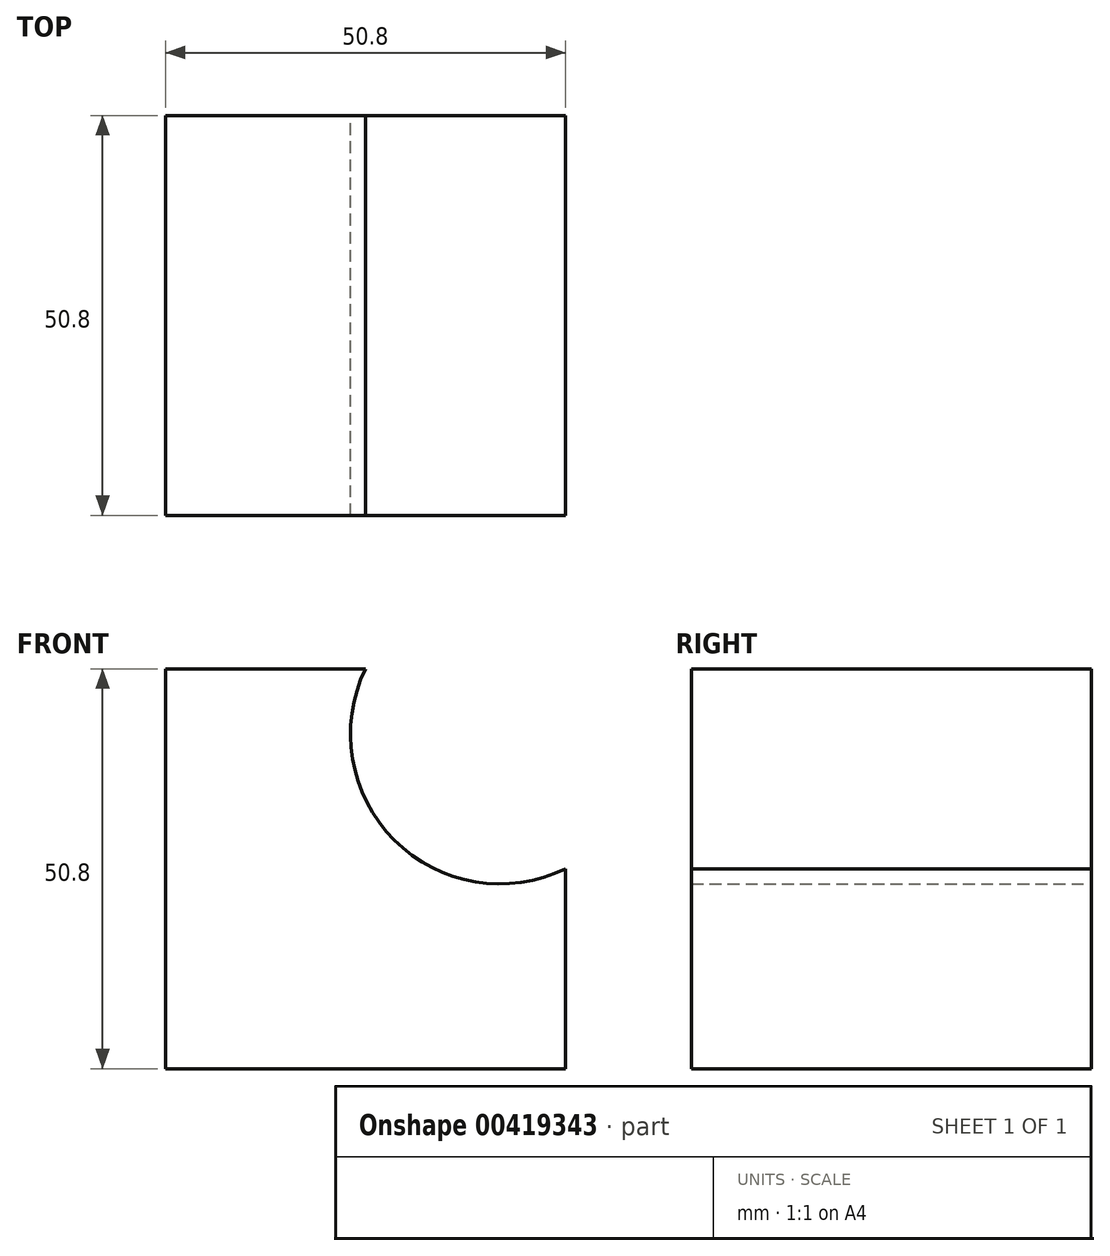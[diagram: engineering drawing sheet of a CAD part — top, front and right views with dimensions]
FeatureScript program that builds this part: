
annotation { "Feature Type Name" : "Feature", "Feature Type Description" : "" }
export const myFeature = defineFeature(function(context is Context, id is Id, definition is map)
    precondition{}
    {
        {
            var Q0;
            Q0=qCreatedBy(makeId("Front.planeOp"),FACE);
            var sketch = newSketch(context, id + "F0", { "sketchPlane" : qUnion([Q0])});
            skLineSegment(sketch, "E0", {"start": v(0, 0) * mm, "end": v(-50.8, 0) * mm});
            skLineSegment(sketch, "E1", {"start": v(-50.8, 0) * mm, "end": v(-50.8, 50.8) * mm});
            skLineSegment(sketch, "E2", {"start": v(-50.8, 50.8) * mm, "end": v(-25.4, 50.8) * mm});
            skLineSegment(sketch, "E3", {"start": v(0, 0) * mm, "end": v(0, 25.4) * mm});
            skArc(sketch, "E4", {"start": v(-25.4, 50.8) * mm, "mid": v(-21.75, 29.05) * mm, "end": v(0, 25.4) * mm});
            skSolve(sketch);
        }
        {
            var Q0;
            Q0 = qSketchRegion(id + "F0", true);
            extrude(context, id + "F1", {"entities" : qUnion([Q0]), "depth" : 50.8 * mm});
        }
    });
